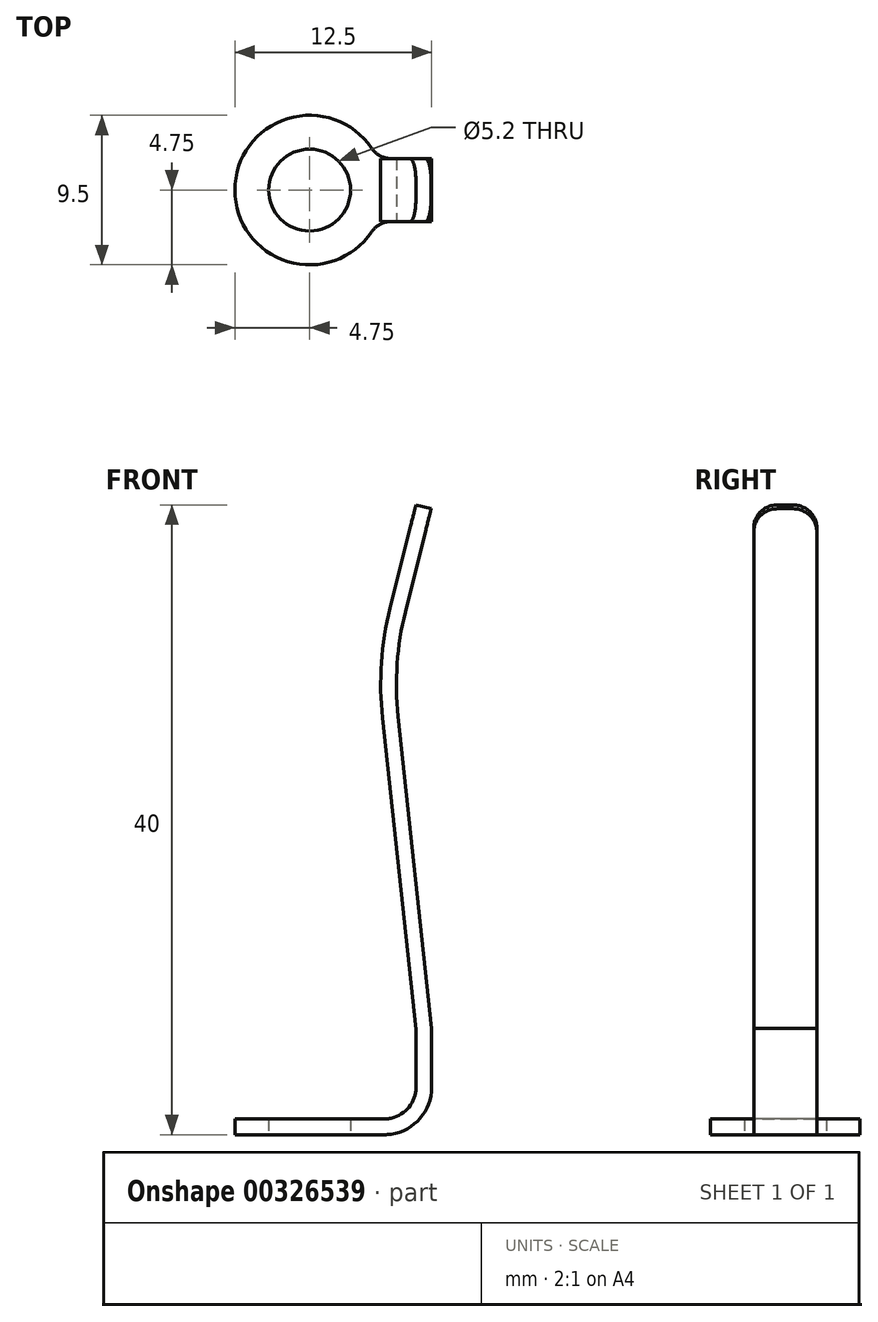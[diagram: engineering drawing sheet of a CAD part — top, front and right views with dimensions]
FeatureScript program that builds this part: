
annotation { "Feature Type Name" : "Feature", "Feature Type Description" : "" }
export const myFeature = defineFeature(function(context is Context, id is Id, definition is map)
    precondition{}
    {
        {
            var Q0;
            Q0=qCreatedBy(makeId("Top.planeOp"),FACE);
            var sketch = newSketch(context, id + "F0", { "sketchPlane" : qUnion([Q0])});
            skCircle(sketch, "E0", {"center": v(0, 0) * mm, "radius": 2.6 * mm});
            skArc(sketch, "E1", {"start": v(4.3, 2) * mm, "mid": v(-4.75, 0) * mm, "end": v(4.3, -2) * mm});
            skLineSegment(sketch, "E2.bottom", {"start": v(8.75, -2) * mm, "end": v(4.3, -2) * mm});
            skLineSegment(sketch, "E2.top", {"start": v(8.75, 2) * mm, "end": v(4.3, 2) * mm});
            skLineSegment(sketch, "E2.left", {"start": v(8.75, -2) * mm, "end": v(8.75, 2) * mm});
            skPoint(sketch, "E2.middle", {"position": v(4.75, 0) * mm});
            skPoint(sketch, "E3.orphan", {"position": v(0.75, 2) * mm});
            skPoint(sketch, "E4.trimOffspring.end.orphan", {"position": v(0.75, -2) * mm});
            skSolve(sketch);
        }
        {
            var Q0;
            Q0=makeQuery(id+"F0.imprint","IMPRINT",FACE,{"disambiguationData":[TD([[makeQuery(id+"F0.imprint","IMPRINT",EDGE,{"derivedFrom":sQuery(id+"F0.wireOp",EDGE,"E0")}),-1.0]])]});
            extrude(context, id + "F1", {"entities" : qUnion([Q0]), "depth" : 40 * mm});
        }
        {
            var Q0;
            Q0=qCreatedBy(makeId("Front.planeOp"),FACE);
            var sketch = newSketch(context, id + "F2", { "sketchPlane" : qUnion([Q0])});
            skLineSegment(sketch, "E5", {"start": v(3.53, 0) * mm, "end": v(-4.2, 0) * mm, "construction": true});
            skLineSegment(sketch, "E6", {"start": v(4.75, 1) * mm, "end": v(-9.1, 1) * mm});
            skLineSegment(sketch, "E7", {"start": v(7.75, 0) * mm, "end": v(7.75, 40) * mm, "construction": true});
            skPoint(sketch, "E8.visualSharp", {"position": v(6.75, 1) * mm});
            skArc(sketch, "E8.filletArc", {"start": v(4.75, 1) * mm, "mid": v(6.16, 1.59) * mm, "end": v(6.75, 3) * mm});
            skLineSegment(sketch, "E9", {"start": v(6.75, 6.7) * mm, "end": v(4.63, 26.47) * mm});
            skLineSegment(sketch, "E10", {"start": v(7.75, 40) * mm, "end": v(6.75, 40) * mm});
            skLineSegment(sketch, "E11", {"start": v(5.11, 33.45) * mm, "end": v(6.75, 40) * mm});
            skPoint(sketch, "E12.visualSharp", {"position": v(4.25, 30) * mm});
            skArc(sketch, "E12.filletArc", {"start": v(5.11, 33.45) * mm, "mid": v(4.56, 29.98) * mm, "end": v(4.63, 26.47) * mm});
            skLineSegment(sketch, "E13", {"start": v(6.75, 3) * mm, "end": v(6.75, 6.7) * mm});
            skLineSegment(sketch, "E14.0", {"start": v(6.08, 33.2) * mm, "end": v(7.72, 39.76) * mm});
            skArc(sketch, "E14.1", {"start": v(6.08, 33.2) * mm, "mid": v(5.56, 29.9) * mm, "end": v(5.62, 26.57) * mm});
            skLineSegment(sketch, "E14.2", {"start": v(4.75, 0) * mm, "end": v(-9.1, 0) * mm});
            skArc(sketch, "E14.3", {"start": v(4.75, 0) * mm, "mid": v(6.87, 0.88) * mm, "end": v(7.75, 3) * mm});
            skLineSegment(sketch, "E14.4", {"start": v(7.75, 3) * mm, "end": v(7.75, 6.75) * mm});
            skLineSegment(sketch, "E14.5", {"start": v(7.75, 6.75) * mm, "end": v(5.62, 26.57) * mm});
            skLineSegment(sketch, "E15", {"start": v(6.75, 40) * mm, "end": v(7.72, 39.76) * mm});
            skLineSegment(sketch, "E16", {"start": v(-9.1, 0) * mm, "end": v(-9.1, -6.06) * mm});
            skLineSegment(sketch, "E17", {"start": v(-9.1, -6.06) * mm, "end": v(12.39, -5.1) * mm});
            skLineSegment(sketch, "E18", {"start": v(12.39, -5.1) * mm, "end": v(10.25, 42.5) * mm});
            skLineSegment(sketch, "E19", {"start": v(10.25, 42.5) * mm, "end": v(5.62, 43.91) * mm});
            skLineSegment(sketch, "E20", {"start": v(5.62, 43.91) * mm, "end": v(6.75, 40) * mm});
            skLineSegment(sketch, "E21", {"start": v(6.75, 40) * mm, "end": v(-4.48, 43.91) * mm});
            skLineSegment(sketch, "E22", {"start": v(-4.48, 43.91) * mm, "end": v(-11.35, 32.94) * mm});
            skLineSegment(sketch, "E23", {"start": v(-11.35, 32.94) * mm, "end": v(-9.1, 1) * mm});
            skLineSegment(sketch, "E24", {"start": v(10.25, 42.5) * mm, "end": v(7.72, 39.76) * mm});
            skLineSegment(sketch, "E25", {"start": v(7.72, 39.76) * mm, "end": v(10.25, 42.5) * mm});
            skSolve(sketch);
        }
        {
            var Q0;
            Q0=makeQuery(id+"F2.imprint","IMPRINT",FACE,{"disambiguationData":[TD([[makeQuery(id+"F2.imprint","IMPRINT",EDGE,{"derivedFrom":sQuery(id+"F2.wireOp",EDGE,"E14.0")}),-1.0]])]});
            var Q1;
            Q1=makeQuery(id+"F2.imprint","IMPRINT",FACE,{"disambiguationData":[TD([[makeQuery(id+"F2.imprint","IMPRINT",EDGE,{"derivedFrom":sQuery(id+"F2.wireOp",EDGE,"E6")}),-1.0]])]});
            var Q2;
            Q2=makeQuery(id+"F2.imprint","IMPRINT",FACE,{"disambiguationData":[TD([[makeQuery(id+"F2.imprint","IMPRINT",EDGE,{"derivedFrom":sQuery(id+"F2.wireOp",EDGE,"E15")}),1.0]])]});
            extrude(context, id + "F3", {"entities" : qUnion([Q0, Q1, Q2]), "operationType" : NewBodyOperationType.REMOVE, "oppositeDirection" : true, "depth" : 25 * mm, "symmetric" : true});
        }
        {
            var Q0;
            Q0=makeQuery(id+"F3.boolean.opBoolean","INTERSECT",EDGE,{"derivedFrom":[makeQuery(id+"F1.opExtrude","SWEPT_FACE",FACE,{"disambiguationData":[OSD([sQuery(id+"F0.wireOp",EDGE,"E2.bottom")])]}),makeQuery(id+"F3.opExtrude","SWEPT_FACE",FACE,{"disambiguationData":[OSD([sQuery(id+"F2.wireOp",EDGE,"E15")])]})]});
            var Q1;
            Q1=makeQuery(id+"F3.boolean.opBoolean","INTERSECT",EDGE,{"derivedFrom":[makeQuery(id+"F1.opExtrude","SWEPT_FACE",FACE,{"disambiguationData":[OSD([sQuery(id+"F0.wireOp",EDGE,"E2.top")])]}),makeQuery(id+"F3.opExtrude","SWEPT_FACE",FACE,{"disambiguationData":[OSD([sQuery(id+"F2.wireOp",EDGE,"E15")])]})]});
            var Q2;
            Q2=makeQuery(id+"F1.opExtrude","SWEPT_EDGE",EDGE,{"disambiguationData":[OSD([sQuery(id+"F0.wireOp",EDGE,"E1"),sQuery(id+"F0.wireOp",EDGE,"E2.bottom")])]});
            var Q3;
            Q3=makeQuery(id+"F1.opExtrude","SWEPT_EDGE",EDGE,{"disambiguationData":[OSD([sQuery(id+"F0.wireOp",EDGE,"E1"),sQuery(id+"F0.wireOp",EDGE,"E2.top")])]});
            fillet(context, id + "F4", {"entities" : qUnion([Q0, Q1, Q2, Q3]), "radius" : 1.5 * mm, "tangentPropagation" : true, "allowEdgeOverflow" : false});
        }
    });
